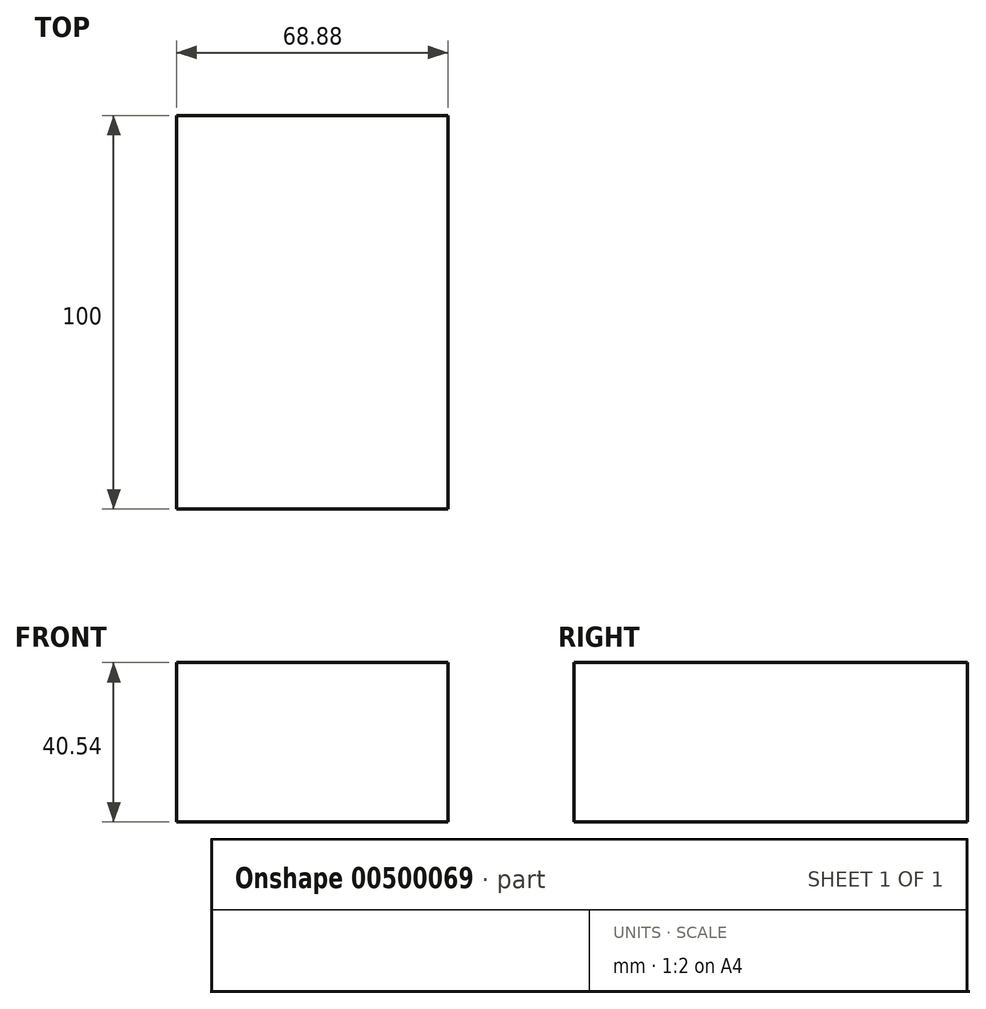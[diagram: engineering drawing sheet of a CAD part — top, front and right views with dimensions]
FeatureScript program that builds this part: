
annotation { "Feature Type Name" : "Feature", "Feature Type Description" : "" }
export const myFeature = defineFeature(function(context is Context, id is Id, definition is map)
    precondition{}
    {
        {
            var Q0;
            Q0=qCreatedBy(makeId("Front.planeOp"),FACE);
            var sketch = newSketch(context, id + "F0", { "sketchPlane" : qUnion([Q0])});
            skLineSegment(sketch, "E0.bottom", {"start": v(34.44, 20.27) * mm, "end": v(-34.44, 20.27) * mm});
            skLineSegment(sketch, "E0.top", {"start": v(34.44, -20.27) * mm, "end": v(-34.44, -20.27) * mm});
            skLineSegment(sketch, "E0.left", {"start": v(34.44, 20.27) * mm, "end": v(34.44, -20.27) * mm});
            skLineSegment(sketch, "E0.right", {"start": v(-34.44, 20.27) * mm, "end": v(-34.44, -20.27) * mm});
            skPoint(sketch, "E0.middle", {"position": v(0, 0) * mm});
            skSolve(sketch);
        }
        {
            var Q0;
            Q0=makeQuery(id+"F0.imprint","IMPRINT",FACE,{"disambiguationData":[TD([[makeQuery(id+"F0.imprint","IMPRINT",EDGE,{"derivedFrom":sQuery(id+"F0.wireOp",EDGE,"E0.bottom")}),1.0]])]});
            extrude(context, id + "F1", {"entities" : qUnion([Q0]), "endBound" : BoundingType.SYMMETRIC, "depth" : 100 * mm});
        }
    });
